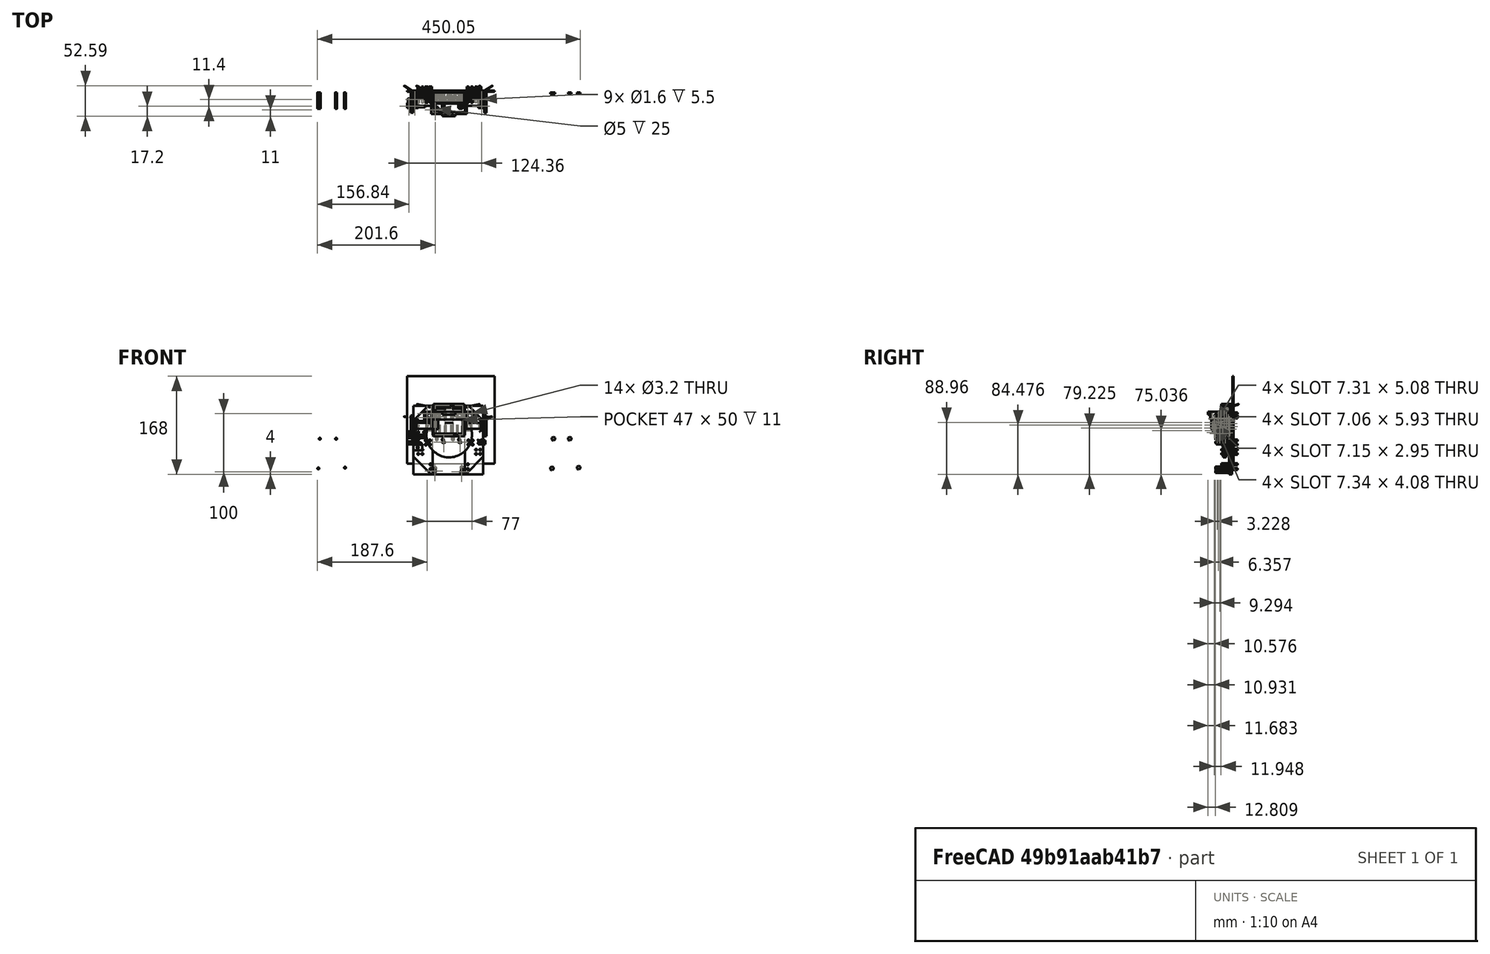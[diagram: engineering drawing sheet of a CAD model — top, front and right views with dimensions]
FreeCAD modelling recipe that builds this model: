
FCSTD DOCUMENT  (FreeCAD 0.17R13522 (Git))
Label: 5028.6 Blank Frank
License: All rights reserved
LicenseURL: http://en.wikipedia.org/wiki/All_rights_reserved
objects: Part::Cylinder×133, Part::Box×78, Part::Fuse×69, Part::Cut×66, Part::Feature×37, Part::MultiFuse×31, Part::Fillet×15, Part::Mirroring×14, Part::Chamfer×10, Part::Cone×9, Part::Compound×3, Part::Torus×2, App::DocumentObjectGroup×1
note: 467 computed .brp shape members not serialized (recipe doc carries the construction recipe); baked Part::Feature solids carry a one-line shape summary decoded from their .brp

FEATURE [Part::Cylinder] Cylinder
  Angle = 360
  AttacherType = Attacher::AttachEngine3D
  Height = 30
  Radius = 7
FEATURE [Part::Cylinder] Cylinder001
  Angle = 360
  AttacherType = Attacher::AttachEngine3D
  Height = 19
  Placement = pos=(0,0,30) rot=(0,0,1;0rad)
  Radius = 7
FEATURE [Part::Cylinder] Cylinder002
  Angle = 360
  AttacherType = Attacher::AttachEngine3D
  Height = 1.8
  Placement = pos=(0,0,49) rot=(0,0,1;0rad)
  Radius = 2.5
FEATURE [Part::Compound] Compound
  Links = -> [Cylinder,Cylinder002,Cylinder001]
FEATURE [Part::Cylinder] Cylinder003
  Angle = 360
  AttacherType = Attacher::AttachEngine3D
  Height = 30
  Radius = 7
FEATURE [Part::Cylinder] Cylinder004
  Angle = 360
  AttacherType = Attacher::AttachEngine3D
  Height = 19
  Placement = pos=(0,0,30) rot=(0,0,1;0rad)
  Radius = 7
FEATURE [Part::Cylinder] Cylinder005
  Angle = 360
  AttacherType = Attacher::AttachEngine3D
  Height = 1.8
  Placement = pos=(0,0,49) rot=(0,0,1;0rad)
  Radius = 2.5
FEATURE [Part::Compound] Compound001
  Links = -> [Cylinder003,Cylinder005,Cylinder004]
  Placement = pos=(14.5,0,50) rot=(1,0,0;3.14159rad)
FEATURE [Part::Cylinder] Cylinder006
  Angle = 360
  AttacherType = Attacher::AttachEngine3D
  Height = 30
  Radius = 7
FEATURE [Part::Cylinder] Cylinder007
  Angle = 360
  AttacherType = Attacher::AttachEngine3D
  Height = 19
  Placement = pos=(0,0,30) rot=(0,0,1;0rad)
  Radius = 7
FEATURE [Part::Cylinder] Cylinder008
  Angle = 360
  AttacherType = Attacher::AttachEngine3D
  Height = 1.8
  Placement = pos=(0,0,49) rot=(0,0,1;0rad)
  Radius = 2.5
FEATURE [Part::Compound] Compound002
  Links = -> [Cylinder006,Cylinder008,Cylinder007]
  Placement = pos=(29,0,0) rot=(0,0,1;0rad)
FEATURE [Part::Box] Box  label="Cube"
  AttacherType = Attacher::AttachEngine3D
  Height = 50
  Length = 47
  Placement = pos=(-9,-8,0) rot=(0,0,1;0rad)
  Width = 12
FEATURE [Part::Box] Box001  label="Cube001"
  AttacherType = Attacher::AttachEngine3D
  Height = 55
  Length = 53
  Placement = pos=(-12,-8,-2.5) rot=(0,0,1;0rad)
  Width = 11
FEATURE [Part::Cylinder] Cylinder009
  Angle = 360
  AttacherType = Attacher::AttachEngine3D
  Height = 50
  Radius = 7
FEATURE [Part::Cylinder] Cylinder010
  Angle = 360
  AttacherType = Attacher::AttachEngine3D
  Height = 50
  Placement = pos=(14.5,0,0) rot=(0,0,1;0rad)
  Radius = 7
FEATURE [Part::Cut] Cut
  Base = -> Box001
  Tool = -> Box
FEATURE [Part::Box] Box002  label="Cube002"
  AttacherType = Attacher::AttachEngine3D
  Height = 55
  Length = 53
  Placement = pos=(-12,3,-2.5) rot=(0,0,1;0rad)
  Width = 7
FEATURE [Part::Fuse] Fusion
  Base = -> Cut
  Tool = -> Box002
FEATURE [Part::Cut] Cut001  label="No idea why this is here...."
  Base = -> Fusion
  Tool = -> Cylinder009
FEATURE [Part::Cylinder] Cylinder011
  Angle = 360
  AttacherType = Attacher::AttachEngine3D
  Height = 50
  Placement = pos=(29,0,0) rot=(0,0,1;0rad)
  Radius = 7
FEATURE [Part::Box] Box003  label="Cube003"
  AttacherType = Attacher::AttachEngine3D
  Height = 5
  Length = 2
  Placement = pos=(28,-9,-2) rot=(0,0,1;0rad)
  Width = 12
FEATURE [Part::Box] Box004  label="Cube004"
  AttacherType = Attacher::AttachEngine3D
  Height = 5
  Length = 2
  Placement = pos=(18.5,-9,46) rot=(0,0,1;0rad)
  Width = 12
FEATURE [Part::Box] Box005  label="Cube005"
  AttacherType = Attacher::AttachEngine3D
  Height = 5
  Length = 2
  Placement = pos=(-2,-9,46) rot=(0,0,1;0rad)
  Width = 12
FEATURE [Part::Box] Box006  label="Cube006"
  AttacherType = Attacher::AttachEngine3D
  Height = 5
  Length = 3
  Placement = pos=(35,-9,-4) rot=(0,0,1;0rad)
  Width = 12
FEATURE [Part::Cut] Cut008
FEATURE [Part::Torus] Torus001
  Angle1 = -180
  Angle2 = 180
  Angle3 = 360
  AttacherType = Attacher::AttachEngine3D
  Placement = pos=(0,0,2) rot=(0,0,1;0rad)
  Radius1 = 19
  Radius2 = 1.5
FEATURE [Part::Cut] Cut009  label="wheel2"
  Base = -> Cut008
  Placement = pos=(75,-7,15) rot=(0,1,0;1.5708rad)
  Tool = -> Torus001
FEATURE [Part::Torus] Torus
  Angle1 = -180
  Angle2 = 180
  Angle3 = 360
  AttacherType = Attacher::AttachEngine3D
  Placement = pos=(0,0,2) rot=(0,0,1;0rad)
  Radius1 = 19
  Radius2 = 1.5
FEATURE [Part::Cut] Cut010
FEATURE [Part::Cut] Cut011  label="wheel1"
  Base = -> Cut010
  Placement = pos=(-51,-7,15) rot=(0,1,0;1.5708rad)
  Tool = -> Torus
FEATURE [Part::Fuse] Fusion003
FEATURE [Part::Cylinder] Cylinder012
  Angle = 360
  AttacherType = Attacher::AttachEngine3D
  Height = 10
  Placement = pos=(5,-4.5,0) rot=(0,1,0;1.5708rad)
  Radius = 0.8
FEATURE [Part::Fuse] Fusion048  label="right-motor001"
  Base = -> Cylinder012
  Placement = pos=(-51,-7,15) rot=(0,0,1;0rad)
  Tool = -> Fusion003
FEATURE [Part::Fuse] Fusion049
FEATURE [Part::Cylinder] Cylinder013
  Angle = 360
  AttacherType = Attacher::AttachEngine3D
  Height = 10
  Placement = pos=(5,-4.5,0) rot=(0,1,0;1.5708rad)
  Radius = 0.8
FEATURE [Part::Fuse] Fusion050  label="left-motor001"
  Base = -> Cylinder013
  Placement = pos=(79,-7,15) rot=(0,0,1;3.14159rad)
  Tool = -> Fusion049
FEATURE [Part::Box] Box007  label="Cube007"
  AttacherType = Attacher::AttachEngine3D
  Height = 5
  Length = 2
  Placement = pos=(37.5,-9,46) rot=(0,0,1;0rad)
  Width = 12
FEATURE [Part::Box] Box008  label="Cube008"
  AttacherType = Attacher::AttachEngine3D
  Height = 5
  Length = 2
  Placement = pos=(8,-9,-2) rot=(0,0,1;0rad)
  Width = 12
FEATURE [Part::Box] Box009  label="The Ground"
  AttacherType = Attacher::AttachEngine3D
  Height = 150
  Length = 150
  Placement = pos=(-57,11,-50) rot=(0,0,1;0rad)
  Width = 2
FEATURE [Part::Box] Box010  label="Motor Mount Left"
  AttacherType = Attacher::AttachEngine3D
  Height = 16
  Length = 4
  Placement = pos=(69,-13,7) rot=(0,0,1;0rad)
  Width = 20
FEATURE [Part::Box] Box011  label="Motor Mount Right"
  AttacherType = Attacher::AttachEngine3D
  Height = 16
  Length = 4
  Placement = pos=(-46,-13,7) rot=(0,0,1;0rad)
  Width = 20
FEATURE [Part::Box] Box012  label="Motor Support Right"
  AttacherType = Attacher::AttachEngine3D
  Height = 16
  Length = 10
  Placement = pos=(-25,-1,7) rot=(0,0,1;0rad)
  Width = 8
FEATURE [Part::Box] Box013  label="Motor Support Left"
  AttacherType = Attacher::AttachEngine3D
  Height = 16
  Length = 10
  Placement = pos=(43,-1,7) rot=(0,0,1;0rad)
  Width = 8
FEATURE [Part::Cylinder] Cylinder014
  Angle = 360
  AttacherType = Attacher::AttachEngine3D
  Height = 28
  Placement = pos=(40.7,0,-10.3) rot=(1,0,0;1.5708rad)
  Radius = 1.6
FEATURE [Part::Cylinder] Cylinder015
  Angle = 360
  AttacherType = Attacher::AttachEngine3D
  Height = 28
  Placement = pos=(-2.4,0,-59.8) rot=(1,0,0;1.5708rad)
  Radius = 1.6
FEATURE [Part::Cylinder] Cylinder016
  Angle = 360
  AttacherType = Attacher::AttachEngine3D
  Height = 28
  Placement = pos=(-5,0,-9) rot=(1,0,0;1.5708rad)
  Radius = 1.6
FEATURE [Part::Cylinder] Cylinder017
  Angle = 360
  AttacherType = Attacher::AttachEngine3D
  Height = 28
  Placement = pos=(25.5,0,-59.8) rot=(1,0,0;1.5708rad)
  Radius = 1.6
FEATURE [Part::Fuse] Fusion051
  Base = -> Cylinder015
  Tool = -> Cylinder016
FEATURE [Part::Fuse] Fusion052
  Base = -> Cylinder014
  Tool = -> Cylinder017
FEATURE [Part::Fuse] Fusion053  label="Screw holes on Arduino Duo"
  Base = -> Fusion051
  Tool = -> Fusion052
FEATURE [Part::Mirroring] Part__Mirroring  label="XXXXXScrew holes on Arduino Duo (Mirror #1)"
  Base = (0,0,0)
  Normal = (0,0,1)
  Placement = pos=(-204,10,-67) rot=(0,0,1;0rad)
  Source = -> Fusion053
FEATURE [Part::Box] Box014  label="Not used Cube"
  AttacherType = Attacher::AttachEngine3D
  Height = 10
  Length = 10
  Placement = pos=(-1,4,-5.85) rot=(0,0,1;0rad)
  Width = 10
FEATURE [Part::Box] Box015  label="Cube014 Arduino Support cube"
  AttacherType = Attacher::AttachEngine3D
  Height = 67
  Length = 55
  Placement = pos=(-13,5,-68) rot=(0,0,1;0rad)
  Width = 5
FEATURE [Part::Cylinder] Cylinder018
  Angle = 360
  AttacherType = Attacher::AttachEngine3D
  Height = 5
  Placement = pos=(15,0,0) rot=(1,0,0;1.5708rad)
  Radius = 39
FEATURE [Part::Cut] Cut014  label="M3 Nut"
  Base = -> Cut001
  Placement = pos=(-6.4,10,-7.2) rot=(1,0,0;1.5708rad)
  Tool = -> Cylinder001
FEATURE [Part::Cut] Cut015  label="M3 Nut001"
  Base = -> Cut001
  Placement = pos=(21.5,10,-7.2) rot=(1,0,0;1.5708rad)
  Tool = -> Cylinder001
FEATURE [Part::Cut] Cut016  label="M3 Nut002"
  Base = -> Cut001
  Placement = pos=(36.7,10,-56.7) rot=(1,0,0;1.5708rad)
  Tool = -> Cylinder001
FEATURE [Part::Cut] Cut017  label="M3 Nut003"
  Base = -> Cut001
  Placement = pos=(-9,10,-58) rot=(1,0,0;1.5708rad)
  Tool = -> Cylinder001
FEATURE [Part::Cut] Cut018
  Base = -> Cut
  Placement = pos=(-9,10,-58) rot=(1,0,0;1.5708rad)
  Tool = -> Box006
FEATURE [Part::Cut] Cut019
  Base = -> Cut
  Placement = pos=(36.7,10,-56.7) rot=(1,0,0;1.5708rad)
  Tool = -> Box006
FEATURE [Part::Cut] Cut020
  Base = -> Cut
  Placement = pos=(-6.4,10,-7.2) rot=(1,0,0;1.5708rad)
  Tool = -> Box006
FEATURE [Part::Cut] Cut021
  Base = -> Cut
  Placement = pos=(21.5,10,-7.2) rot=(1,0,0;1.5708rad)
  Tool = -> Box006
FEATURE [Part::MultiFuse] Fusion054  label="XXXXXHex Holes"
  Placement = pos=(200,0,0) rot=(0,0,1;0rad)
  Shapes = -> [Cut018,Cut021,Cut019,Cut020]
FEATURE [Part::Box] Box016  label="Cube015"
  AttacherType = Attacher::AttachEngine3D
  Height = 117
  Length = 33
  Placement = pos=(-46,7,-68) rot=(0,0,1;0rad)
  Width = 3
FEATURE [Part::Box] Box017  label="Cube016"
  AttacherType = Attacher::AttachEngine3D
  Height = 117
  Length = 31
  Placement = pos=(42,7,-68) rot=(0,0,1;0rad)
  Width = 3
FEATURE [Part::Cylinder] Cylinder019
  Angle = 360
  AttacherType = Attacher::AttachEngine3D
  Height = 28
  Placement = pos=(48,20,-10) rot=(1,0,0;1.5708rad)
  Radius = 1.6
FEATURE [Part::Cylinder] Cylinder020
  Angle = 360
  AttacherType = Attacher::AttachEngine3D
  Height = 28
  Placement = pos=(47,20,-51) rot=(1,0,0;1.5708rad)
  Radius = 1.6
FEATURE [Part::Cylinder] Cylinder021
  Angle = 360
  AttacherType = Attacher::AttachEngine3D
  Height = 28
  Placement = pos=(48,20,-17) rot=(1,0,0;1.5708rad)
  Radius = 1.6
FEATURE [Part::Cylinder] Cylinder022
  Angle = 360
  AttacherType = Attacher::AttachEngine3D
  Height = 28
  Placement = pos=(47,20,-59) rot=(1,0,0;1.5708rad)
  Radius = 1.6
FEATURE [Part::Cylinder] Cylinder023
  Angle = 360
  AttacherType = Attacher::AttachEngine3D
  Height = 28
  Placement = pos=(55,20,-17) rot=(1,0,0;1.5708rad)
  Radius = 1.6
FEATURE [Part::Cylinder] Cylinder024
  Angle = 360
  AttacherType = Attacher::AttachEngine3D
  Height = 28
  Placement = pos=(55,20,-10) rot=(1,0,0;1.5708rad)
  Radius = 1.6
FEATURE [Part::MultiFuse] Fusion055
  Shapes = -> [Cylinder021,Cylinder023,Cylinder024,Cylinder019]
FEATURE [Part::MultiFuse] Fusion056
  Placement = pos=(13,0,-16) rot=(0,0,1;0rad)
  Shapes = -> [Cylinder021,Cylinder023,Cylinder024,Cylinder019]
FEATURE [Part::MultiFuse] Fusion057  label="Mount holes top left"
  Placement = pos=(-1,0,46) rot=(0,0,1;0rad)
  Shapes = -> [Cylinder021,Cylinder023,Cylinder024,Cylinder019]
FEATURE [Part::MultiFuse] Fusion058  label="Mount holes top right"
  Placement = pos=(-71,0,46) rot=(0,0,1;0rad)
  Shapes = -> [Cylinder021,Cylinder023,Cylinder024,Cylinder019]
FEATURE [Part::MultiFuse] Fusion059
  Shapes = -> [Cylinder022,Cylinder020,Fusion055,Fusion056]
FEATURE [Part::Mirroring] Part__Mirroring001  label="Mount holes bottom right"
  Base = (0,0,0)
  Normal = (1,0,0)
  Placement = pos=(30,0,0) rot=(0,0,1;0rad)
  Source = -> Fusion059
FEATURE [Part::Cylinder] Cylinder025
  Angle = 360
  AttacherType = Attacher::AttachEngine3D
  Height = 28
  Placement = pos=(48,20,-10) rot=(1,0,0;1.5708rad)
  Radius = 1.6
FEATURE [Part::Cylinder] Cylinder026
  Angle = 360
  AttacherType = Attacher::AttachEngine3D
  Height = 28
  Placement = pos=(47,20,-51) rot=(1,0,0;1.5708rad)
  Radius = 1.6
FEATURE [Part::Cylinder] Cylinder027
  Angle = 360
  AttacherType = Attacher::AttachEngine3D
  Height = 28
  Placement = pos=(48,20,-17) rot=(1,0,0;1.5708rad)
  Radius = 1.6
FEATURE [Part::Cylinder] Cylinder028
  Angle = 360
  AttacherType = Attacher::AttachEngine3D
  Height = 28
  Placement = pos=(47,20,-59) rot=(1,0,0;1.5708rad)
  Radius = 1.6
FEATURE [Part::Cylinder] Cylinder029
  Angle = 360
  AttacherType = Attacher::AttachEngine3D
  Height = 28
  Placement = pos=(55,20,-17) rot=(1,0,0;1.5708rad)
  Radius = 1.6
FEATURE [Part::Cylinder] Cylinder030
  Angle = 360
  AttacherType = Attacher::AttachEngine3D
  Height = 28
  Placement = pos=(55,20,-10) rot=(1,0,0;1.5708rad)
  Radius = 1.6
FEATURE [Part::MultiFuse] Fusion060
  Shapes = -> [Cylinder027,Cylinder029,Cylinder030,Cylinder025]
FEATURE [Part::MultiFuse] Fusion061
  Placement = pos=(13,0,-16) rot=(0,0,1;0rad)
  Shapes = -> [Cylinder027,Cylinder029,Cylinder030,Cylinder025]
FEATURE [Part::MultiFuse] Fusion062  label="Mount holes bottom left"
  Shapes = -> [Cylinder028,Cylinder026,Fusion060,Fusion061]
FEATURE [Part::Cylinder] Cylinder031  label="Cylinder127"
  Angle = 360
  AttacherType = Attacher::AttachEngine3D
  Height = 10
  Placement = pos=(0,18,29) rot=(0,0,1;0rad)
  Radius = 2.25
FEATURE [Part::Cylinder] Cylinder032  label="Cylinder128"
  Angle = 360
  AttacherType = Attacher::AttachEngine3D
  Height = 10
  Placement = pos=(4.5,18,32) rot=(0,0,1;0rad)
  Radius = 1
FEATURE [Part::Cylinder] Cylinder033  label="Cylinder129"
  Angle = 360
  AttacherType = Attacher::AttachEngine3D
  Height = 10
  Placement = pos=(-4.5,18,32) rot=(0,0,1;0rad)
  Radius = 1
FEATURE [Part::Fuse] Fusion009  label="Mounting Screw Holes"
  Base = -> Cylinder032
  Tool = -> Cylinder033
FEATURE [Part::Fuse] Fusion071  label="Motor Holes Left"
  Base = -> Cylinder031
  Placement = pos=(37,-7,-3) rot=(0.57735,0.57735,0.57735;2.0944rad)
  Tool = -> Fusion009
FEATURE [Part::Cylinder] Cylinder034  label="Cylinder130"
  Angle = 360
  AttacherType = Attacher::AttachEngine3D
  Height = 10
  Placement = pos=(0,18,29) rot=(0,0,1;0rad)
  Radius = 2.25
FEATURE [Part::Cylinder] Cylinder035  label="Cylinder131"
  Angle = 360
  AttacherType = Attacher::AttachEngine3D
  Height = 10
  Placement = pos=(4.5,18,32) rot=(0,0,1;0rad)
  Radius = 1
FEATURE [Part::Cylinder] Cylinder036  label="Cylinder132"
  Angle = 360
  AttacherType = Attacher::AttachEngine3D
  Height = 10
  Placement = pos=(-4.5,18,32) rot=(0,0,1;0rad)
  Radius = 1
FEATURE [Part::Fuse] Fusion072  label="Mounting Screw Holes001"
  Base = -> Cylinder035
  Tool = -> Cylinder036
FEATURE [Part::Fuse] Fusion073  label="Motor Holes Right"
  Base = -> Cylinder034
  Placement = pos=(-79,-7,-3) rot=(0.57735,0.57735,0.57735;2.0944rad)
  Tool = -> Fusion072
FEATURE [Part::Cylinder] Cylinder037  label="Cylinder133"
  Angle = 360
  AttacherType = Attacher::AttachEngine3D
  Height = 28
  Placement = pos=(40.7,0,-10.3) rot=(1,0,0;1.5708rad)
  Radius = 1.6
FEATURE [Part::Cylinder] Cylinder038  label="Cylinder134"
  Angle = 360
  AttacherType = Attacher::AttachEngine3D
  Height = 28
  Placement = pos=(-2.4,0,-59.8) rot=(1,0,0;1.5708rad)
  Radius = 1.6
FEATURE [Part::Cylinder] Cylinder039  label="Cylinder135"
  Angle = 360
  AttacherType = Attacher::AttachEngine3D
  Height = 28
  Placement = pos=(-5,0,-9) rot=(1,0,0;1.5708rad)
  Radius = 1.6
FEATURE [Part::Cylinder] Cylinder040  label="Cylinder136"
  Angle = 360
  AttacherType = Attacher::AttachEngine3D
  Height = 28
  Placement = pos=(25.5,0,-59.8) rot=(1,0,0;1.5708rad)
  Radius = 1.6
FEATURE [Part::Fuse] Fusion074
  Base = -> Cylinder038
  Tool = -> Cylinder039
FEATURE [Part::Fuse] Fusion075
  Base = -> Cylinder037
  Tool = -> Cylinder040
FEATURE [Part::Fuse] Fusion076  label="Screw holes on Arduino Duo001"
  Base = -> Fusion074
  Tool = -> Fusion075
FEATURE [Part::Mirroring] Part__Mirroring002  label="Screw holes on Arduino Duo (Mirror #1)001"
  Base = (0,0,0)
  Normal = (0,0,1)
  Placement = pos=(-4,10,-67) rot=(0,0,1;0rad)
  Source = -> Fusion076
FEATURE [Part::Mirroring] Part__Mirroring003  label="Screw holes on Arduino Duo (Mirror #1)001 (Mirror #4)"
  Base = (0,0,0)
  Normal = (1,0,0)
  Placement = pos=(27,0,-6) rot=(0,0,1;0rad)
  Source = -> Part__Mirroring002
FEATURE [Part::Box] Box018  label="Cube017"
  AttacherType = Attacher::AttachEngine3D
  Height = 50
  Length = 47
  Placement = pos=(-9,-8,0) rot=(0,0,1;0rad)
  Width = 12
FEATURE [Part::Box] Box019  label="Cube018"
  AttacherType = Attacher::AttachEngine3D
  Height = 55
  Length = 53
  Placement = pos=(-12,-8,-2.5) rot=(0,0,1;0rad)
  Width = 11
FEATURE [Part::Cut] Cut031
  Base = -> Box019
  Tool = -> Box018
FEATURE [Part::Box] Box020  label="Cube019"
  AttacherType = Attacher::AttachEngine3D
  Height = 5
  Length = 3
  Placement = pos=(35,-9,-4) rot=(0,0,1;0rad)
  Width = 12
FEATURE [Part::Cut] Cut032
  Base = -> Cut031
  Placement = pos=(-9,10,-58) rot=(1,0,0;1.5708rad)
  Tool = -> Box020
FEATURE [Part::Cut] Cut033
  Base = -> Cut031
  Placement = pos=(36.7,10,-56.7) rot=(1,0,0;1.5708rad)
  Tool = -> Box020
FEATURE [Part::Cut] Cut034
  Base = -> Cut031
  Placement = pos=(-6.4,10,-7.2) rot=(1,0,0;1.5708rad)
  Tool = -> Box020
FEATURE [Part::Cut] Cut035
  Base = -> Cut031
  Placement = pos=(21.5,10,-7.2) rot=(1,0,0;1.5708rad)
  Tool = -> Box020
FEATURE [Part::MultiFuse] Fusion077
  Shapes = -> [Cut032,Cut035,Cut033,Cut034]
FEATURE [Part::Mirroring] Part__Mirroring004  label="Hex Holes"
  Base = (0,0,0)
  Normal = (1,0,0)
  Placement = pos=(27,0,-6) rot=(0,0,1;0rad)
  Source = -> Fusion077
FEATURE [Part::Box] Box021  label="Cube020"
  AttacherType = Attacher::AttachEngine3D
  Height = 13
  Length = 61
  Placement = pos=(-16,-27,26) rot=(0,0,1;0rad)
  Width = 34
FEATURE [Part::Box] Box022  label="Cube021"
  AttacherType = Attacher::AttachEngine3D
  Height = 13
  Length = 12
  Placement = pos=(45,4,26) rot=(0,0,1;0rad)
  Width = 3
FEATURE [Part::Box] Box023  label="Cube022"
  AttacherType = Attacher::AttachEngine3D
  Height = 13
  Length = 12
  Placement = pos=(-28,4,26) rot=(0,0,1;0rad)
  Width = 3
FEATURE [Part::Box] Box024  label="Cube023"
  AttacherType = Attacher::AttachEngine3D
  Height = 13
  Length = 55
  Placement = pos=(-13,-24,26) rot=(0,0,1;0rad)
  Width = 31
FEATURE [Part::Cylinder] Cylinder041  label="Cylinder137"
  Angle = 360
  AttacherType = Attacher::AttachEngine3D
  Height = 28
  Placement = pos=(54,20,29) rot=(1,0,0;1.5708rad)
  Radius = 1.6
FEATURE [Part::Cylinder] Cylinder042  label="Cylinder138"
  Angle = 360
  AttacherType = Attacher::AttachEngine3D
  Height = 28
  Placement = pos=(54,20,36) rot=(1,0,0;1.5708rad)
  Radius = 1.6
FEATURE [Part::Cylinder] Cylinder043  label="Cylinder139"
  Angle = 360
  AttacherType = Attacher::AttachEngine3D
  Height = 28
  Placement = pos=(-23,20,29) rot=(1,0,0;1.5708rad)
  Radius = 1.6
FEATURE [Part::Cylinder] Cylinder044  label="Cylinder140"
  Angle = 360
  AttacherType = Attacher::AttachEngine3D
  Height = 28
  Placement = pos=(-23,20,36) rot=(1,0,0;1.5708rad)
  Radius = 1.6
FEATURE [Part::Cylinder] Cylinder045  label="Cylinder141"
  Angle = 360
  AttacherType = Attacher::AttachEngine3D
  Height = 10
  Placement = pos=(36,-17.25,32.5) rot=(0,1,0;1.5708rad)
  Radius = 2.5
FEATURE [Part::Cut] Cut037
  Base = -> Box021
  Tool = -> Box024
FEATURE [Part::Cut] Cut038
  Base = -> Cut037
  Tool = -> Cylinder045
FEATURE [Part::Box] Box025  label="Cube024"
  AttacherType = Attacher::AttachEngine3D
  Height = 5
  Length = 22
  Placement = pos=(3.5,-31,34) rot=(0,0,1;0rad)
  Width = 4
FEATURE [Part::Cylinder] Cylinder046  label="Cylinder142"
  Angle = 360
  AttacherType = Attacher::AttachEngine3D
  Height = 10
  Placement = pos=(20.75,-29,30) rot=(0,0,1;0rad)
  Radius = 0.85
FEATURE [Part::Cylinder] Cylinder047  label="Cylinder143"
  Angle = 360
  AttacherType = Attacher::AttachEngine3D
  Height = 10
  Placement = pos=(8.25,-29,40) rot=(1,0,0;3.14159rad)
  Radius = 0.85
FEATURE [Part::Fuse] Fusion078
  Base = -> Cylinder046
  Tool = -> Cylinder047
FEATURE [Part::Cut] Cut039
  Base = -> Box025
  Tool = -> Fusion078
FEATURE [Part::Fuse] Fusion079
  Base = -> Cut038
  Tool = -> Cut039
FEATURE [Part::Fuse] Fusion080
  Base = -> Cylinder043
  Tool = -> Cylinder044
FEATURE [Part::Fuse] Fusion081
  Base = -> Cylinder041
  Tool = -> Cylinder042
FEATURE [Part::Fuse] Fusion082
  Base = -> Box023
  Tool = -> Fusion079
FEATURE [Part::Fuse] Fusion083
  Base = -> Box022
  Tool = -> Fusion082
FEATURE [Part::Cut] Cut040
  Base = -> Fusion083
  Tool = -> Fusion081
FEATURE [Part::Cut] Cut041  label="Switch Bracket"
  Base = -> Cut040
  Tool = -> Fusion080
FEATURE [Part::Cylinder] Cylinder048  label="Cylinder144"
  Angle = 360
  AttacherType = Attacher::AttachEngine3D
  Height = 28
  Placement = pos=(-23,20,29) rot=(1,0,0;1.5708rad)
  Radius = 1.6
FEATURE [Part::Cylinder] Cylinder049  label="Cylinder145"
  Angle = 360
  AttacherType = Attacher::AttachEngine3D
  Height = 28
  Placement = pos=(-23,20,36) rot=(1,0,0;1.5708rad)
  Radius = 1.6
FEATURE [Part::Fuse] Fusion084
  Base = -> Cylinder048
  Placement = pos=(1,0,0) rot=(0,0,1;0rad)
  Tool = -> Cylinder049
FEATURE [Part::Cylinder] Cylinder050  label="Cylinder146"
  Angle = 360
  AttacherType = Attacher::AttachEngine3D
  Height = 28
  Placement = pos=(-23,20,29) rot=(1,0,0;1.5708rad)
  Radius = 1.6
FEATURE [Part::Cylinder] Cylinder051  label="Cylinder147"
  Angle = 360
  AttacherType = Attacher::AttachEngine3D
  Height = 28
  Placement = pos=(-23,20,36) rot=(1,0,0;1.5708rad)
  Radius = 1.6
FEATURE [Part::Fuse] Fusion085
  Base = -> Cylinder050
  Placement = pos=(-1,0,0) rot=(0,0,1;0rad)
  Tool = -> Cylinder051
FEATURE [Part::Cut] Cut042
  Base = -> Cut041
  Tool = -> Fusion084
FEATURE [Part::Cut] Cut043  label="Switch Bracket001"
  Base = -> Cut042
  Tool = -> Fusion085
FEATURE [Part::Cylinder] Cylinder052  label="Cylinder148"
  Angle = 360
  AttacherType = Attacher::AttachEngine3D
  Height = 42
  Radius = 4.8
FEATURE [Part::Cylinder] Cylinder053  label="Cylinder149"
  Angle = 360
  AttacherType = Attacher::AttachEngine3D
  Height = 1.6
  Placement = pos=(0,0,42) rot=(0,0,1;0rad)
  Radius = 1.65
FEATURE [Part::Fuse] Fusion086
  Base = -> Cylinder052
  Placement = pos=(2,0,0) rot=(0,0,1;0rad)
  Tool = -> Cylinder053
FEATURE [Part::Cylinder] Cylinder054  label="Cylinder150"
  Angle = 360
  AttacherType = Attacher::AttachEngine3D
  Height = 42
  Radius = 4.8
FEATURE [Part::Cylinder] Cylinder055  label="Cylinder151"
  Angle = 360
  AttacherType = Attacher::AttachEngine3D
  Height = 1.6
  Placement = pos=(0,0,42) rot=(0,0,1;0rad)
  Radius = 1.65
FEATURE [Part::Fuse] Fusion087
  Base = -> Cylinder054
  Placement = pos=(12,0,0) rot=(0,0,1;0rad)
  Tool = -> Cylinder055
FEATURE [Part::Cylinder] Cylinder056  label="Cylinder152"
  Angle = 360
  AttacherType = Attacher::AttachEngine3D
  Height = 42
  Radius = 4.8
FEATURE [Part::Cylinder] Cylinder057  label="Cylinder153"
  Angle = 360
  AttacherType = Attacher::AttachEngine3D
  Height = 1.6
  Placement = pos=(0,0,42) rot=(0,0,1;0rad)
  Radius = 1.65
FEATURE [Part::Fuse] Fusion088
  Base = -> Cylinder056
  Placement = pos=(22,0,0) rot=(0,0,1;0rad)
  Tool = -> Cylinder057
FEATURE [Part::Cylinder] Cylinder058  label="Cylinder154"
  Angle = 360
  AttacherType = Attacher::AttachEngine3D
  Height = 42
  Radius = 4.8
FEATURE [Part::Cylinder] Cylinder059  label="Cylinder155"
  Angle = 360
  AttacherType = Attacher::AttachEngine3D
  Height = 1.6
  Placement = pos=(0,0,42) rot=(0,0,1;0rad)
  Radius = 1.65
FEATURE [Part::Fuse] Fusion089
  Base = -> Cylinder058
  Placement = pos=(32,0,0) rot=(0,0,1;0rad)
  Tool = -> Cylinder059
FEATURE [Part::Cylinder] Cylinder060  label="Cylinder156"
  Angle = 360
  AttacherType = Attacher::AttachEngine3D
  Height = 42
  Radius = 4.8
FEATURE [Part::Cylinder] Cylinder061  label="Cylinder157"
  Angle = 360
  AttacherType = Attacher::AttachEngine3D
  Height = 1.6
  Placement = pos=(0,0,42) rot=(0,0,1;0rad)
  Radius = 1.65
FEATURE [Part::Fuse] Fusion093
  Base = -> Cylinder060
  Placement = pos=(-8,0,0) rot=(0,0,1;0rad)
  Tool = -> Cylinder061
FEATURE [Part::MultiFuse] Fusion094  label="AAA Batts"
  Placement = pos=(2.5,0,2) rot=(0,0,1;0rad)
  Shapes = -> [Fusion093,Fusion086,Fusion087,Fusion088,Fusion089]
FEATURE [Part::Cylinder] Cylinder062  label="Cylinder158"
  Angle = 360
  AttacherType = Attacher::AttachEngine3D
  Height = 10
  Radius = 17
FEATURE [Part::Cylinder] Cylinder063  label="Cylinder159"
  Angle = 360
  AttacherType = Attacher::AttachEngine3D
  Height = 16
  Placement = pos=(0,0,-4) rot=(0,0,1;0rad)
  Radius = 10
FEATURE [Part::Cut] Cut044
  Base = -> Cylinder062
  Tool = -> Cylinder063
FEATURE [Part::Box] Box026  label="Cube025"
  AttacherType = Attacher::AttachEngine3D
  Height = 20
  Length = 18
  Placement = pos=(0,0,-5) rot=(0,0,1;0rad)
  Width = 20
FEATURE [Part::Box] Box027  label="Cube026"
  AttacherType = Attacher::AttachEngine3D
  Height = 20
  Length = 10
  Placement = pos=(0,0,-5) rot=(0,0,1;0.174533rad)
  Width = 20
FEATURE [Part::Cut] Cut045
  Base = -> Box027
  Tool = -> Box026
FEATURE [Part::Feature] Cut045001
  Placement = pos=(0,0,0) rot=(0,0,1;0.349066rad)
  shape: bbox 10 x 22.32 x 20 mm, 7 faces (baked)
FEATURE [Part::Feature] Cut045002
  Placement = pos=(0,0,0) rot=(0,0,1;0.698132rad)
  shape: bbox 15.32 x 20.52 x 20 mm, 7 faces (baked)
FEATURE [Part::Feature] Cut045003
  Placement = pos=(0,0,0) rot=(0,0,1;1.0472rad)
  shape: bbox 18.79 x 16.24 x 20 mm, 7 faces (baked)
FEATURE [Part::Feature] Cut045004
  Placement = pos=(0,0,0) rot=(0,0,1;1.39626rad)
  shape: bbox 20 x 10 x 20 mm, 7 faces (baked)
FEATURE [Part::Feature] Cut045005
  Placement = pos=(0,0,0) rot=(0,0,1;1.74533rad)
  shape: bbox 22.21 x 9.894 x 20 mm, 7 faces (baked)
FEATURE [Part::Feature] Cut045006
  Placement = pos=(0,0,0) rot=(0,0,1;2.0944rad)
  shape: bbox 21.75 x 12.86 x 20 mm, 7 faces (baked)
FEATURE [Part::Feature] Cut045007
  Placement = pos=(0,0,0) rot=(0,0,1;2.44346rad)
  shape: bbox 18.66 x 17.32 x 20 mm, 7 faces (baked)
FEATURE [Part::Feature] Cut045008
  Placement = pos=(0,0,0) rot=(0,0,1;2.79253rad)
  shape: bbox 13.32 x 19.7 x 20 mm, 7 faces (baked)
FEATURE [Part::Feature] Cut045009
  Placement = pos=(0,0,0) rot=(0,0,1;3.14159rad)
  shape: bbox 10.1 x 21.43 x 20 mm, 7 faces (baked)
FEATURE [Part::Feature] Cut045010
  Placement = pos=(0,0,0) rot=(0,0,1;3.49066rad)
  shape: bbox 10 x 22.32 x 20 mm, 7 faces (baked)
FEATURE [Part::Feature] Cut045011
  Placement = pos=(0,0,0) rot=(0,0,1;3.83972rad)
  shape: bbox 15.32 x 20.52 x 20 mm, 7 faces (baked)
FEATURE [Part::Feature] Cut045012
  Placement = pos=(0,0,0) rot=(0,0,1;4.18879rad)
  shape: bbox 18.79 x 16.24 x 20 mm, 7 faces (baked)
FEATURE [Part::Feature] Cut045013
  Placement = pos=(0,0,0) rot=(0,0,-1;1.74533rad)
  shape: bbox 20 x 10 x 20 mm, 7 faces (baked)
FEATURE [Part::Feature] Cut045014
  Placement = pos=(0,0,0) rot=(0,0,-1;1.39626rad)
  shape: bbox 22.21 x 9.894 x 20 mm, 7 faces (baked)
FEATURE [Part::Feature] Cut045015
  Placement = pos=(0,0,0) rot=(0,0,-1;1.0472rad)
  shape: bbox 21.75 x 12.86 x 20 mm, 7 faces (baked)
FEATURE [Part::Feature] Cut045016
  Placement = pos=(0,0,0) rot=(0,0,-1;0.698132rad)
  shape: bbox 18.66 x 17.32 x 20 mm, 7 faces (baked)
FEATURE [Part::Feature] Cut045017
  Placement = pos=(0,0,0) rot=(0,0,-1;0.349066rad)
  shape: bbox 13.32 x 19.7 x 20 mm, 7 faces (baked)
FEATURE [Part::MultiFuse] Fusion095
  Shapes = -> [Cut045001,Cut045008,Cut045010,Cut045009,Cut045005,Cut045003,Cut045006,Cut045002,Cut045004,Cut045007,Cut045016,Cut045017,Cut045011,Cut045012,Cut045013,Cut045014,Cut045015,Cut045]
FEATURE [Part::Cut] Cut045018
  Base = -> Cut044
  Placement = pos=(72,-7,15) rot=(0,1,0;1.5708rad)
  Tool = -> Fusion095
FEATURE [Part::Cut] Cut045019  label="Wheel with Spokes AB"
  Base = -> Cut009
  Tool = -> Cut045018
FEATURE [Part::Box] Box028  label="Cube027"
  AttacherType = Attacher::AttachEngine3D
  Height = 5
  Length = 2
  Placement = pos=(37.5,-9,-2) rot=(0,0,1;0rad)
  Width = 12
FEATURE [Part::Box] Box029  label="Cube028"
  AttacherType = Attacher::AttachEngine3D
  Height = 50
  Length = 47
  Placement = pos=(-9,-8,0) rot=(0,0,1;0rad)
  Width = 12
FEATURE [Part::Box] Box030  label="Cube029"
  AttacherType = Attacher::AttachEngine3D
  Height = 55
  Length = 53
  Placement = pos=(-12,-8,-2.5) rot=(0,0,1;0rad)
  Width = 11
FEATURE [Part::Cylinder] Cylinder064  label="Cylinder160"
  Angle = 360
  AttacherType = Attacher::AttachEngine3D
  Height = 50
  Radius = 7
FEATURE [Part::Cut] Cut045020
  Base = -> Box030
  Tool = -> Box029
FEATURE [Part::Box] Box031  label="Cube030"
  AttacherType = Attacher::AttachEngine3D
  Height = 55
  Length = 53
  Placement = pos=(-12,3,-2.5) rot=(0,0,1;0rad)
  Width = 7
FEATURE [Part::Fuse] Fusion096
  Base = -> Cut045020
  Tool = -> Box031
FEATURE [Part::Box] Box032  label="Battery Base"
  AttacherType = Attacher::AttachEngine3D
  Height = 50
  Length = 55
  Placement = pos=(-13,3,-1) rot=(0,0,1;0rad)
  Width = 7
FEATURE [Part::Box] Box033  label="Cube031"
  AttacherType = Attacher::AttachEngine3D
  Height = 30
  Length = 10
  Placement = pos=(-14,-25,9) rot=(0,0,1;0rad)
  Width = 10
FEATURE [Part::Cylinder] Cylinder065  label="Cylinder161"
  Angle = 360
  AttacherType = Attacher::AttachEngine3D
  Height = 43.5
  Placement = pos=(4,0,2) rot=(0,0,1;0rad)
  Radius = 4.8
FEATURE [Part::Cylinder] Cylinder066  label="Cylinder162"
  Angle = 360
  AttacherType = Attacher::AttachEngine3D
  Height = 1.6
  Placement = pos=(4,0,44) rot=(0,0,1;0rad)
  Radius = 1.65
FEATURE [Part::Fuse] Fusion097
  Base = -> Cylinder065
  Tool = -> Cylinder066
FEATURE [Part::Cylinder] Cylinder067  label="Cylinder163"
  Angle = 360
  AttacherType = Attacher::AttachEngine3D
  Height = 43.5
  Placement = pos=(14,0,2) rot=(0,0,1;0rad)
  Radius = 4.8
FEATURE [Part::Cylinder] Cylinder068  label="Cylinder164"
  Angle = 360
  AttacherType = Attacher::AttachEngine3D
  Height = 1.6
  Placement = pos=(14,0,44) rot=(0,0,1;0rad)
  Radius = 1.65
FEATURE [Part::Fuse] Fusion098
  Base = -> Cylinder067
  Tool = -> Cylinder068
FEATURE [Part::Cylinder] Cylinder069  label="Cylinder165"
  Angle = 360
  AttacherType = Attacher::AttachEngine3D
  Height = 43.5
  Placement = pos=(24,0,2) rot=(0,0,1;0rad)
  Radius = 4.8
FEATURE [Part::Cylinder] Cylinder070  label="Cylinder166"
  Angle = 360
  AttacherType = Attacher::AttachEngine3D
  Height = 1.6
  Placement = pos=(24,0,44) rot=(0,0,1;0rad)
  Radius = 1.65
FEATURE [Part::Fuse] Fusion099
  Base = -> Cylinder069
  Tool = -> Cylinder070
FEATURE [Part::Cylinder] Cylinder071  label="Cylinder167"
  Angle = 360
  AttacherType = Attacher::AttachEngine3D
  Height = 43.5
  Placement = pos=(34,0,2) rot=(0,0,1;0rad)
  Radius = 4.8
FEATURE [Part::Cylinder] Cylinder072  label="Cylinder168"
  Angle = 360
  AttacherType = Attacher::AttachEngine3D
  Height = 1.6
  Placement = pos=(34,0,44) rot=(0,0,1;0rad)
  Radius = 1.65
FEATURE [Part::Fuse] Fusion100
  Base = -> Cylinder071
  Tool = -> Cylinder072
FEATURE [Part::Cylinder] Cylinder073  label="Cylinder169"
  Angle = 360
  AttacherType = Attacher::AttachEngine3D
  Height = 43.5
  Placement = pos=(-6,0,2) rot=(0,0,1;0rad)
  Radius = 4.8
FEATURE [Part::Cylinder] Cylinder074  label="Cylinder170"
  Angle = 360
  AttacherType = Attacher::AttachEngine3D
  Height = 1.6
  Placement = pos=(-6,0,44) rot=(0,0,1;0rad)
  Radius = 1.65
FEATURE [Part::Fuse] Fusion101
  Base = -> Cylinder073
  Tool = -> Cylinder074
FEATURE [Part::MultiFuse] Fusion102  label="AAA Batts001"
  Shapes = -> [Fusion101,Fusion097,Fusion098,Fusion099,Fusion100]
FEATURE [Part::Cylinder] Cylinder075  label="Cylinder171"
  Angle = 360
  AttacherType = Attacher::AttachEngine3D
  Height = 10
  Placement = pos=(-9,-20,4) rot=(0,0,1;0rad)
  Radius = 2.75
FEATURE [Part::Cylinder] Cylinder076  label="Cylinder172"
  Angle = 360
  AttacherType = Attacher::AttachEngine3D
  Height = 27
  Placement = pos=(-9,-20,14) rot=(0,0,1;0rad)
  Radius = 2.5
FEATURE [Part::Fuse] Fusion103  label="phototransistor hole"
  Base = -> Cylinder075
  Tool = -> Cylinder076
FEATURE [Part::Cut] Cut045021  label="Phototransistor holder"
  Base = -> Box033
  Tool = -> Fusion103
FEATURE [Part::Fuse] Fusion104  label="Switch Mount with phototransistor hole"
  Base = -> Cut043
  Tool = -> Cut045021
FEATURE [Part::Cut] Cut045022
  Base = -> Box032
  Tool = -> Fusion102
FEATURE [Part::Box] Box034  label="Cube032"
  AttacherType = Attacher::AttachEngine3D
  Height = 2.5
  Length = 55
  Placement = pos=(-13,-9,-1) rot=(0,0,1;0rad)
  Width = 12
FEATURE [Part::Box] Box035  label="Cube033"
  AttacherType = Attacher::AttachEngine3D
  Height = 2.5
  Length = 55
  Placement = pos=(-13,-9,46.5) rot=(0,0,1;0rad)
  Width = 12
FEATURE [Part::Box] Box036  label="Cube034"
  AttacherType = Attacher::AttachEngine3D
  Height = 50
  Length = 2.5
  Placement = pos=(-13,-9,-1) rot=(0,0,1;0rad)
  Width = 12
FEATURE [Part::Box] Box037  label="Cube035"
  AttacherType = Attacher::AttachEngine3D
  Height = 50
  Length = 2.5
  Placement = pos=(39.5,-9,-1) rot=(0,0,1;0rad)
  Width = 12
FEATURE [Part::MultiFuse] Fusion105
  Shapes = -> [Box034,Box036,Box037,Box035]
FEATURE [Part::Box] Box038  label="Cube036"
  AttacherType = Attacher::AttachEngine3D
  Height = 5
  Length = 2
  Placement = pos=(-10.5,-9,46) rot=(0,0,1;0rad)
  Width = 12
FEATURE [Part::Box] Box039  label="Cube037"
  AttacherType = Attacher::AttachEngine3D
  Height = 5
  Length = 2
  Placement = pos=(-10.5,-9,-2) rot=(0,0,1;0rad)
  Width = 12
FEATURE [Part::MultiFuse] Fusion106
  Shapes = -> [Box039,Box038,Box028,Box007]
FEATURE [Part::MultiFuse] Fusion107
  Shapes = -> [Box003,Box004,Box005,Box008]
FEATURE [Part::Cut] Cut045023
  Base = -> Fusion105
  Tool = -> Fusion106
FEATURE [Part::Cut] Cut045024
  Base = -> Cut045023
  Tool = -> Fusion107
FEATURE [Part::Box] Box040  label="Cube038"
  AttacherType = Attacher::AttachEngine3D
  Height = 1.6
  Length = 30
  Placement = pos=(-56,-15.5,-6) rot=(0,0,1;0rad)
  Width = 15
FEATURE [Part::Box] Box041  label="Cube039"
  AttacherType = Attacher::AttachEngine3D
  Height = 10
  Length = 14
  Placement = pos=(-56,-10.5,-4.5) rot=(0,0,1;0rad)
  Width = 6
FEATURE [Part::Box] Box042  label="Cube040"
  AttacherType = Attacher::AttachEngine3D
  Height = 10
  Length = 5.3
  Placement = pos=(-51.7,-11.5,-4.5) rot=(0,0,1;0rad)
  Width = 8
FEATURE [Part::Cut] Cut045025
  Base = -> Box041
  Tool = -> Box042
FEATURE [Part::Fuse] Fusion108  label="Spoke Sensor PCB"
  Base = -> Box040
  Tool = -> Cut045025
FEATURE [Part::Cylinder] Cylinder077  label="Cylinder173"
  Angle = 360
  AttacherType = Attacher::AttachEngine3D
  Height = 14.5
  Placement = pos=(-43.6,-2.4,-9) rot=(0,0,1;0rad)
  Radius = 0.8
FEATURE [Part::Cylinder] Cylinder078  label="Cylinder174"
  Angle = 360
  AttacherType = Attacher::AttachEngine3D
  Height = 14.5
  Placement = pos=(-43.6,-13.8,-9) rot=(0,0,1;0rad)
  Radius = 0.8
FEATURE [Part::Fuse] Fusion109
  Base = -> Cylinder077
  Tool = -> Cylinder078
FEATURE [Part::Cut] Cut045026  label="Spoke Sensor PCB001"
  Base = -> Fusion108
  Tool = -> Fusion109
FEATURE [Part::Cylinder] Cylinder079  label="Cylinder175"
  Angle = 360
  AttacherType = Attacher::AttachEngine3D
  Height = 14.5
  Placement = pos=(-43.6,-2.4,-18) rot=(0,0,1;0rad)
  Radius = 0.8
FEATURE [Part::Cylinder] Cylinder080  label="Cylinder176"
  Angle = 360
  AttacherType = Attacher::AttachEngine3D
  Height = 14.5
  Placement = pos=(-43.6,-13.8,-18) rot=(0,0,1;0rad)
  Radius = 0.8
FEATURE [Part::Fuse] Fusion110  label="Batt Holder"
  Base = -> Cut045022
  Tool = -> Cut045024
FEATURE [Part::Box] Box043  label="Cube041"
  AttacherType = Attacher::AttachEngine3D
  Height = 4
  Length = 12
  Placement = pos=(-50,-16.75,-17) rot=(0,0,1;0rad)
  Width = 23.75
FEATURE [Part::Cone] Cone
  Angle = 360
  AttacherType = Attacher::AttachEngine3D
  Height = 1.5
  Placement = pos=(-43.6,-2.4,-13) rot=(0,0,1;0rad)
  Radius1 = 2.75
  Radius2 = 1.25
FEATURE [Part::Cone] Cone001
  Angle = 360
  AttacherType = Attacher::AttachEngine3D
  Height = 1.5
  Placement = pos=(-43.6,-13.8,-13) rot=(0,0,1;0rad)
  Radius1 = 2.75
  Radius2 = 1.25
FEATURE [Part::Fuse] Fusion111
  Base = -> Cone
  Tool = -> Cone001
FEATURE [Part::Fuse] Fusion113
  Base = -> Cylinder079
  Tool = -> Cylinder080
FEATURE [Part::Cylinder] Cylinder081  label="Cylinder177"
  Angle = 360
  AttacherType = Attacher::AttachEngine3D
  Height = 14.5
  Placement = pos=(-43.6,-2.4,-18) rot=(0,0,1;0rad)
  Radius = 0.8
FEATURE [Part::Cylinder] Cylinder082  label="Cylinder178"
  Angle = 360
  AttacherType = Attacher::AttachEngine3D
  Height = 14.5
  Placement = pos=(-43.6,-13.8,-18) rot=(0,0,1;0rad)
  Radius = 0.8
FEATURE [Part::Box] Box044  label="Cube042"
  AttacherType = Attacher::AttachEngine3D
  Height = 4
  Length = 12
  Placement = pos=(-50,-16.75,-17) rot=(0,0,1;0rad)
  Width = 26.75
FEATURE [Part::Chamfer] Chamfer001
  Base = -> Box044
  Edges = 1 edges r=7: [Edge3]
FEATURE [Part::Cone] Cone002
  Angle = 360
  AttacherType = Attacher::AttachEngine3D
  Height = 1.5
  Placement = pos=(-43.6,-2.4,-13) rot=(0,0,1;0rad)
  Radius1 = 2.75
  Radius2 = 1.25
FEATURE [Part::Cone] Cone003
  Angle = 360
  AttacherType = Attacher::AttachEngine3D
  Height = 1.5
  Placement = pos=(-43.6,-13.8,-13) rot=(0,0,1;0rad)
  Radius1 = 2.75
  Radius2 = 1.25
FEATURE [Part::Fuse] Fusion114
  Base = -> Cone002
  Tool = -> Cone003
FEATURE [Part::Fuse] Fusion115
  Base = -> Chamfer001
  Tool = -> Fusion114
FEATURE [Part::Fuse] Fusion116
  Base = -> Cylinder081
  Tool = -> Cylinder082
FEATURE [Part::Cut] Cut045028
  Base = -> Fusion115
  Tool = -> Fusion116
FEATURE [Part::Mirroring] Part__Mirroring005  label="Cut045028 (Mirror #6)"
  Base = (0,0,0)
  Normal = (1,0,0)
  Placement = pos=(27,0,0) rot=(0,0,1;0rad)
  Source = -> Cut045028
FEATURE [App::DocumentObjectGroup] Group  label="Older version parts"
  Group = -> [Compound,Compound001,Compound002,Cylinder064,Cylinder010,Cylinder011,Fusion096,Part__Mirroring,Fusion054,Part__Mirroring004,Cut014,Cut015,Cut016,Cut017,Box012,Box013,Box010,Part__Mirroring005]
FEATURE [Part::Box] Box045  label="Cube043"
  AttacherType = Attacher::AttachEngine3D
  Height = 5
  Length = 2
  Placement = pos=(28,-9,-2) rot=(0,0,1;0rad)
  Width = 12
FEATURE [Part::Box] Box046  label="Cube044"
  AttacherType = Attacher::AttachEngine3D
  Height = 5
  Length = 2
  Placement = pos=(18.5,-9,46) rot=(0,0,1;0rad)
  Width = 12
FEATURE [Part::Box] Box047  label="Cube045"
  AttacherType = Attacher::AttachEngine3D
  Height = 5
  Length = 2
  Placement = pos=(-2,-9,46) rot=(0,0,1;0rad)
  Width = 12
FEATURE [Part::Box] Box048  label="Cube046"
  AttacherType = Attacher::AttachEngine3D
  Height = 5
  Length = 2
  Placement = pos=(37.5,-9,46) rot=(0,0,1;0rad)
  Width = 12
FEATURE [Part::Box] Box049  label="Cube047"
  AttacherType = Attacher::AttachEngine3D
  Height = 5
  Length = 2
  Placement = pos=(8,-9,-2) rot=(0,0,1;0rad)
  Width = 12
FEATURE [Part::Box] Box050  label="Motor Mount Left001"
  AttacherType = Attacher::AttachEngine3D
  Height = 16
  Length = 4
  Placement = pos=(69,-13,7) rot=(0,0,1;0rad)
  Width = 20
FEATURE [Part::Box] Box051  label="Motor Mount Right001"
  AttacherType = Attacher::AttachEngine3D
  Height = 16
  Length = 4
  Placement = pos=(-46,-13,7) rot=(0,0,1;0rad)
  Width = 20
FEATURE [Part::Box] Box052  label="Motor Support Right001"
  AttacherType = Attacher::AttachEngine3D
  Height = 16
  Length = 10
  Placement = pos=(-25,-1,7) rot=(0,0,1;0rad)
  Width = 8
FEATURE [Part::Box] Box053  label="Motor Support Left001"
  AttacherType = Attacher::AttachEngine3D
  Height = 16
  Length = 10
  Placement = pos=(43,-1,7) rot=(0,0,1;0rad)
  Width = 8
FEATURE [Part::Box] Box054  label="Cube014 Arduino Support cube001"
  AttacherType = Attacher::AttachEngine3D
  Height = 67
  Length = 55
  Placement = pos=(-13,5,-68) rot=(0,0,1;0rad)
  Width = 5
FEATURE [Part::Box] Box055  label="Cube048"
  AttacherType = Attacher::AttachEngine3D
  Height = 117
  Length = 33
  Placement = pos=(-46,7,-68) rot=(0,0,1;0rad)
  Width = 3
FEATURE [Part::Box] Box056  label="Cube049"
  AttacherType = Attacher::AttachEngine3D
  Height = 117
  Length = 31
  Placement = pos=(42,7,-68) rot=(0,0,1;0rad)
  Width = 3
FEATURE [Part::Cylinder] Cylinder083  label="Cylinder179"
  Angle = 360
  AttacherType = Attacher::AttachEngine3D
  Height = 28
  Placement = pos=(48,20,-10) rot=(1,0,0;1.5708rad)
  Radius = 1.6
FEATURE [Part::Cylinder] Cylinder084  label="Cylinder180"
  Angle = 360
  AttacherType = Attacher::AttachEngine3D
  Height = 28
  Placement = pos=(48,20,-17) rot=(1,0,0;1.5708rad)
  Radius = 1.6
FEATURE [Part::Cylinder] Cylinder085  label="Cylinder181"
  Angle = 360
  AttacherType = Attacher::AttachEngine3D
  Height = 28
  Placement = pos=(55,20,-17) rot=(1,0,0;1.5708rad)
  Radius = 1.6
FEATURE [Part::Cylinder] Cylinder086  label="Cylinder182"
  Angle = 360
  AttacherType = Attacher::AttachEngine3D
  Height = 28
  Placement = pos=(55,20,-10) rot=(1,0,0;1.5708rad)
  Radius = 1.6
FEATURE [Part::MultiFuse] Fusion117  label="Mount holes top left001"
  Placement = pos=(-1,0,46) rot=(0,0,1;0rad)
  Shapes = -> [Cylinder084,Cylinder085,Cylinder086,Cylinder083]
FEATURE [Part::MultiFuse] Fusion118  label="Mount holes top right001"
  Placement = pos=(-71,0,46) rot=(0,0,1;0rad)
  Shapes = -> [Cylinder084,Cylinder085,Cylinder086,Cylinder083]
FEATURE [Part::Cylinder] Cylinder087  label="Cylinder183"
  Angle = 360
  AttacherType = Attacher::AttachEngine3D
  Height = 10
  Placement = pos=(0,18,29) rot=(0,0,1;0rad)
  Radius = 2.25
FEATURE [Part::Cylinder] Cylinder088  label="Cylinder184"
  Angle = 360
  AttacherType = Attacher::AttachEngine3D
  Height = 10
  Placement = pos=(4.5,18,32) rot=(0,0,1;0rad)
  Radius = 1
FEATURE [Part::Cylinder] Cylinder089  label="Cylinder185"
  Angle = 360
  AttacherType = Attacher::AttachEngine3D
  Height = 10
  Placement = pos=(-4.5,18,32) rot=(0,0,1;0rad)
  Radius = 1
FEATURE [Part::Fuse] Fusion119  label="Mounting Screw Holes002"
  Base = -> Cylinder088
  Tool = -> Cylinder089
FEATURE [Part::Fuse] Fusion120  label="Motor Holes Left001"
  Base = -> Cylinder087
  Placement = pos=(37,-7,-3) rot=(0.57735,0.57735,0.57735;2.0944rad)
  Tool = -> Fusion119
FEATURE [Part::Cylinder] Cylinder090  label="Cylinder186"
  Angle = 360
  AttacherType = Attacher::AttachEngine3D
  Height = 10
  Placement = pos=(0,18,29) rot=(0,0,1;0rad)
  Radius = 2.25
FEATURE [Part::Cylinder] Cylinder091  label="Cylinder187"
  Angle = 360
  AttacherType = Attacher::AttachEngine3D
  Height = 10
  Placement = pos=(4.5,18,32) rot=(0,0,1;0rad)
  Radius = 1
FEATURE [Part::Cylinder] Cylinder092  label="Cylinder188"
  Angle = 360
  AttacherType = Attacher::AttachEngine3D
  Height = 10
  Placement = pos=(-4.5,18,32) rot=(0,0,1;0rad)
  Radius = 1
FEATURE [Part::Fuse] Fusion121  label="Mounting Screw Holes003"
  Base = -> Cylinder091
  Tool = -> Cylinder092
FEATURE [Part::Fuse] Fusion122  label="Motor Holes Right001"
  Base = -> Cylinder090
  Placement = pos=(-79,-7,-3) rot=(0.57735,0.57735,0.57735;2.0944rad)
  Tool = -> Fusion121
FEATURE [Part::Cylinder] Cylinder093  label="Cylinder189"
  Angle = 360
  AttacherType = Attacher::AttachEngine3D
  Height = 28
  Placement = pos=(40.7,0,-10.3) rot=(1,0,0;1.5708rad)
  Radius = 1.6
FEATURE [Part::Cylinder] Cylinder094  label="Cylinder190"
  Angle = 360
  AttacherType = Attacher::AttachEngine3D
  Height = 28
  Placement = pos=(-2.4,0,-59.8) rot=(1,0,0;1.5708rad)
  Radius = 1.6
FEATURE [Part::Cylinder] Cylinder095  label="Cylinder191"
  Angle = 360
  AttacherType = Attacher::AttachEngine3D
  Height = 28
  Placement = pos=(-5,0,-9) rot=(1,0,0;1.5708rad)
  Radius = 1.6
FEATURE [Part::Cylinder] Cylinder096  label="Cylinder192"
  Angle = 360
  AttacherType = Attacher::AttachEngine3D
  Height = 28
  Placement = pos=(25.5,0,-59.8) rot=(1,0,0;1.5708rad)
  Radius = 1.6
FEATURE [Part::Fuse] Fusion123
  Base = -> Cylinder094
  Tool = -> Cylinder095
FEATURE [Part::Fuse] Fusion124
  Base = -> Cylinder093
  Tool = -> Cylinder096
FEATURE [Part::Fuse] Fusion125  label="Screw holes on Arduino Duo002"
  Base = -> Fusion123
  Tool = -> Fusion124
FEATURE [Part::Mirroring] Part__Mirroring006  label="Screw holes on Arduino Duo (Mirror #1)002"
  Base = (0,0,0)
  Normal = (0,0,1)
  Placement = pos=(-4,10,-67) rot=(0,0,1;0rad)
  Source = -> Fusion125
FEATURE [Part::Mirroring] Part__Mirroring007  label="Screw holes on Arduino Duo (Mirror #1)001 (Mirror #4)001"
  Base = (0,0,0)
  Normal = (1,0,0)
  Placement = pos=(27,0,-6) rot=(0,0,1;0rad)
  Source = -> Part__Mirroring006
FEATURE [Part::Box] Box057  label="Cube050"
  AttacherType = Attacher::AttachEngine3D
  Height = 50
  Length = 47
  Placement = pos=(-9,-8,0) rot=(0,0,1;0rad)
  Width = 12
FEATURE [Part::Box] Box058  label="Cube051"
  AttacherType = Attacher::AttachEngine3D
  Height = 55
  Length = 53
  Placement = pos=(-12,-8,-2.5) rot=(0,0,1;0rad)
  Width = 11
FEATURE [Part::Cut] Cut045029
  Base = -> Box058
  Tool = -> Box057
FEATURE [Part::Box] Box059  label="Cube052"
  AttacherType = Attacher::AttachEngine3D
  Height = 5
  Length = 3
  Placement = pos=(35,-9,-4) rot=(0,0,1;0rad)
  Width = 12
FEATURE [Part::Cut] Cut045030
  Base = -> Cut045029
  Placement = pos=(-9,10,-58) rot=(1,0,0;1.5708rad)
  Tool = -> Box059
FEATURE [Part::Cut] Cut045031
  Base = -> Cut045029
  Placement = pos=(36.7,10,-56.7) rot=(1,0,0;1.5708rad)
  Tool = -> Box059
FEATURE [Part::Cut] Cut045032
  Base = -> Cut045029
  Placement = pos=(-6.4,10,-7.2) rot=(1,0,0;1.5708rad)
  Tool = -> Box059
FEATURE [Part::Cut] Cut045033
  Base = -> Cut045029
  Placement = pos=(21.5,10,-7.2) rot=(1,0,0;1.5708rad)
  Tool = -> Box059
FEATURE [Part::MultiFuse] Fusion126
  Shapes = -> [Cut045030,Cut045033,Cut045031,Cut045032]
FEATURE [Part::Mirroring] Part__Mirroring008  label="Hex Holes001"
  Base = (0,0,0)
  Normal = (1,0,0)
  Placement = pos=(27,0,-6) rot=(0,0,1;0rad)
  Source = -> Fusion126
FEATURE [Part::Box] Box060  label="Cube053"
  AttacherType = Attacher::AttachEngine3D
  Height = 5
  Length = 2
  Placement = pos=(37.5,-9,-2) rot=(0,0,1;0rad)
  Width = 12
FEATURE [Part::Box] Box061  label="Battery Base001"
  AttacherType = Attacher::AttachEngine3D
  Height = 50
  Length = 55
  Placement = pos=(-13,3,-1) rot=(0,0,1;0rad)
  Width = 7
FEATURE [Part::Cylinder] Cylinder097  label="Cylinder193"
  Angle = 360
  AttacherType = Attacher::AttachEngine3D
  Height = 42
  Radius = 4.8
FEATURE [Part::Cylinder] Cylinder098  label="Cylinder194"
  Angle = 360
  AttacherType = Attacher::AttachEngine3D
  Height = 1.6
  Placement = pos=(0,0,42) rot=(0,0,1;0rad)
  Radius = 1.65
FEATURE [Part::Fuse] Fusion127
  Base = -> Cylinder097
  Placement = pos=(2,0,0) rot=(0,0,1;0rad)
  Tool = -> Cylinder098
FEATURE [Part::Cylinder] Cylinder099  label="Cylinder195"
  Angle = 360
  AttacherType = Attacher::AttachEngine3D
  Height = 42
  Radius = 4.8
FEATURE [Part::Cylinder] Cylinder100  label="Cylinder196"
  Angle = 360
  AttacherType = Attacher::AttachEngine3D
  Height = 1.6
  Placement = pos=(0,0,42) rot=(0,0,1;0rad)
  Radius = 1.65
FEATURE [Part::Fuse] Fusion128
  Base = -> Cylinder099
  Placement = pos=(12,0,0) rot=(0,0,1;0rad)
  Tool = -> Cylinder100
FEATURE [Part::Cylinder] Cylinder101  label="Cylinder197"
  Angle = 360
  AttacherType = Attacher::AttachEngine3D
  Height = 42
  Radius = 4.8
FEATURE [Part::Cylinder] Cylinder102  label="Cylinder198"
  Angle = 360
  AttacherType = Attacher::AttachEngine3D
  Height = 1.6
  Placement = pos=(0,0,42) rot=(0,0,1;0rad)
  Radius = 1.65
FEATURE [Part::Fuse] Fusion129
  Base = -> Cylinder101
  Placement = pos=(22,0,0) rot=(0,0,1;0rad)
  Tool = -> Cylinder102
FEATURE [Part::Cylinder] Cylinder103  label="Cylinder199"
  Angle = 360
  AttacherType = Attacher::AttachEngine3D
  Height = 42
  Radius = 4.8
FEATURE [Part::Cylinder] Cylinder104  label="Cylinder200"
  Angle = 360
  AttacherType = Attacher::AttachEngine3D
  Height = 1.6
  Placement = pos=(0,0,42) rot=(0,0,1;0rad)
  Radius = 1.65
FEATURE [Part::Fuse] Fusion130
  Base = -> Cylinder103
  Placement = pos=(32,0,0) rot=(0,0,1;0rad)
  Tool = -> Cylinder104
FEATURE [Part::Cylinder] Cylinder105  label="Cylinder201"
  Angle = 360
  AttacherType = Attacher::AttachEngine3D
  Height = 42
  Radius = 4.8
FEATURE [Part::Cylinder] Cylinder106  label="Cylinder202"
  Angle = 360
  AttacherType = Attacher::AttachEngine3D
  Height = 1.6
  Placement = pos=(0,0,42) rot=(0,0,1;0rad)
  Radius = 1.65
FEATURE [Part::Fuse] Fusion131
  Base = -> Cylinder105
  Placement = pos=(-8,0,0) rot=(0,0,1;0rad)
  Tool = -> Cylinder106
FEATURE [Part::MultiFuse] Fusion132  label="AAA Batts002"
  Placement = pos=(2,0,2) rot=(0,0,1;0rad)
  Shapes = -> [Fusion131,Fusion127,Fusion128,Fusion129,Fusion130]
FEATURE [Part::Cut] Cut045034
  Base = -> Box061
  Tool = -> Fusion132
FEATURE [Part::Box] Box062  label="Cube054"
  AttacherType = Attacher::AttachEngine3D
  Height = 2.5
  Length = 55
  Placement = pos=(-13,-9,-1) rot=(0,0,1;0rad)
  Width = 12
FEATURE [Part::Box] Box063  label="Cube055"
  AttacherType = Attacher::AttachEngine3D
  Height = 2.5
  Length = 55
  Placement = pos=(-13,-9,46.5) rot=(0,0,1;0rad)
  Width = 12
FEATURE [Part::Box] Box064  label="Cube056"
  AttacherType = Attacher::AttachEngine3D
  Height = 50
  Length = 2.5
  Placement = pos=(-13,-9,-1) rot=(0,0,1;0rad)
  Width = 12
FEATURE [Part::Box] Box065  label="Cube057"
  AttacherType = Attacher::AttachEngine3D
  Height = 50
  Length = 2.5
  Placement = pos=(39.5,-9,-1) rot=(0,0,1;0rad)
  Width = 12
FEATURE [Part::MultiFuse] Fusion133
  Shapes = -> [Box062,Box064,Box065,Box063]
FEATURE [Part::Box] Box066  label="Cube058"
  AttacherType = Attacher::AttachEngine3D
  Height = 5
  Length = 2
  Placement = pos=(-10.5,-9,46) rot=(0,0,1;0rad)
  Width = 12
FEATURE [Part::Box] Box067  label="Cube059"
  AttacherType = Attacher::AttachEngine3D
  Height = 5
  Length = 2
  Placement = pos=(-10.5,-9,-2) rot=(0,0,1;0rad)
  Width = 12
FEATURE [Part::MultiFuse] Fusion134
  Shapes = -> [Box067,Box066,Box060,Box048]
FEATURE [Part::MultiFuse] Fusion135
  Shapes = -> [Box045,Box046,Box047,Box049]
FEATURE [Part::Cut] Cut045035
  Base = -> Fusion133
  Tool = -> Fusion134
FEATURE [Part::Cut] Cut045036
  Base = -> Cut045035
  Tool = -> Fusion135
FEATURE [Part::Cylinder] Cylinder107  label="Cylinder203"
  Angle = 360
  AttacherType = Attacher::AttachEngine3D
  Height = 14.5
  Placement = pos=(-43.6,-2.4,-15) rot=(0,0,1;0rad)
  Radius = 0.8
FEATURE [Part::Cylinder] Cylinder108  label="Cylinder204"
  Angle = 360
  AttacherType = Attacher::AttachEngine3D
  Height = 14.5
  Placement = pos=(-43.6,-13.8,-15) rot=(0,0,1;0rad)
  Radius = 0.8
FEATURE [Part::Fuse] Fusion136
  Base = -> Cut045034
  Tool = -> Cut045036
FEATURE [Part::Box] Box068  label="Cube060"
  AttacherType = Attacher::AttachEngine3D
  Height = 4
  Length = 12
  Placement = pos=(-50,-16.75,-14) rot=(0,0,1;0rad)
  Width = 26.75
FEATURE [Part::Chamfer] Chamfer002
  Base = -> Box068
  Edges = 1 edges r=7: [Edge3]
FEATURE [Part::Cone] Cone004
  Angle = 360
  AttacherType = Attacher::AttachEngine3D
  Height = 1.5
  Placement = pos=(-43.6,-2.4,-10) rot=(0,0,1;0rad)
  Radius1 = 2.75
  Radius2 = 1.25
FEATURE [Part::Cone] Cone005
  Angle = 360
  AttacherType = Attacher::AttachEngine3D
  Height = 1.5
  Placement = pos=(-43.6,-13.8,-10) rot=(0,0,1;0rad)
  Radius1 = 2.75
  Radius2 = 1.25
FEATURE [Part::Fuse] Fusion137
  Base = -> Cone004
  Tool = -> Cone005
FEATURE [Part::Fuse] Fusion138
  Base = -> Chamfer002
  Tool = -> Fusion137
FEATURE [Part::Fuse] Fusion139
  Base = -> Cylinder107
  Tool = -> Cylinder108
FEATURE [Part::Cut] Cut045037
  Base = -> Fusion138
  Tool = -> Fusion139
FEATURE [Part::Cylinder] Cylinder109  label="Cylinder205"
  Angle = 360
  AttacherType = Attacher::AttachEngine3D
  Height = 14.5
  Placement = pos=(-43.6,-2.4,-15) rot=(0,0,1;0rad)
  Radius = 0.8
FEATURE [Part::Cylinder] Cylinder110  label="Cylinder206"
  Angle = 360
  AttacherType = Attacher::AttachEngine3D
  Height = 14.5
  Placement = pos=(-43.6,-13.8,-15) rot=(0,0,1;0rad)
  Radius = 0.8
FEATURE [Part::Box] Box069  label="Cube061"
  AttacherType = Attacher::AttachEngine3D
  Height = 4
  Length = 12
  Placement = pos=(-50,-16.75,-14) rot=(0,0,1;0rad)
  Width = 26.75
FEATURE [Part::Chamfer] Chamfer003
  Base = -> Box069
  Edges = 1 edges r=7: [Edge3]
FEATURE [Part::Cone] Cone006
  Angle = 360
  AttacherType = Attacher::AttachEngine3D
  Height = 1.5
  Placement = pos=(-43.6,-2.4,-10) rot=(0,0,1;0rad)
  Radius1 = 2.75
  Radius2 = 1.25
FEATURE [Part::Cone] Cone007
  Angle = 360
  AttacherType = Attacher::AttachEngine3D
  Height = 1.5
  Placement = pos=(-43.6,-13.8,-10) rot=(0,0,1;0rad)
  Radius1 = 2.75
  Radius2 = 1.25
FEATURE [Part::Fuse] Fusion140
  Base = -> Cone006
  Tool = -> Cone007
FEATURE [Part::Fuse] Fusion141
  Base = -> Chamfer003
  Tool = -> Fusion140
FEATURE [Part::Fuse] Fusion142
  Base = -> Cylinder109
  Tool = -> Cylinder110
FEATURE [Part::Cut] Cut045038
  Base = -> Fusion141
  Tool = -> Fusion142
FEATURE [Part::Mirroring] Part__Mirroring009  label="Cut045028 (Mirror #6)001"
  Base = (0,0,0)
  Normal = (1,0,0)
  Placement = pos=(27,0,0) rot=(0,0,1;0rad)
  Source = -> Cut045038
FEATURE [Part::Cut] Cut045039
  Base = -> Box050
  Tool = -> Fusion120
FEATURE [Part::Cut] Cut045040
  Base = -> Box051
  Tool = -> Fusion122
FEATURE [Part::MultiFuse] Fusion143
  Shapes = -> [Box054,Box055,Box056]
FEATURE [Part::Fuse] Fusion144
  Base = -> Fusion136
  Tool = -> Fusion143
FEATURE [Part::MultiFuse] Fusion145
  Shapes = -> [Fusion144,Cut045040,Cut045039]
FEATURE [Part::MultiFuse] Fusion146
  Shapes = -> [Fusion145,Part__Mirroring009,Cut045037]
FEATURE [Part::Cut] Cut045041
  Base = -> Fusion146
  Tool = -> Fusion117
FEATURE [Part::Cut] Cut045042
  Base = -> Cut045041
  Tool = -> Fusion118
FEATURE [Part::Cut] Cut045043
  Base = -> Cut045042
  Tool = -> Part__Mirroring007
FEATURE [Part::Cut] Cut045044
  Base = -> Cut045043
  Tool = -> Part__Mirroring008
FEATURE [Part::MultiFuse] Fusion147
  Shapes = -> [Cut045044,Box053,Box052]
FEATURE [Part::Chamfer] Chamfer004
  Base = -> Fusion147
  Edges = 1 edges r=25: [Edge43]
FEATURE [Part::Chamfer] Chamfer005
  Base = -> Chamfer004
  Edges = 1 edges r=25: [Edge225]
FEATURE [Part::Chamfer] Chamfer006
  Base = -> Chamfer005
  Edges = 1 edges r=30: [Edge58]
FEATURE [Part::Chamfer] Chamfer007
  Base = -> Chamfer006
  Edges = 1 edges r=30: [Edge148]
FEATURE [Part::Fillet] Fillet
  Base = -> Chamfer007
  Edges = 1 edges r=2: [Edge233]
FEATURE [Part::Fillet] Fillet001
  Base = -> Fillet
  Edges = 1 edges r=2: [Edge6]
FEATURE [Part::Fillet] Fillet002
  Base = -> Fillet001
  Edges = 1 edges r=2: [Edge2]
FEATURE [Part::Fillet] Fillet003
  Base = -> Fillet002
  Edges = 1 edges r=2: [Edge357]
FEATURE [Part::Fillet] Fillet004
  Base = -> Fillet003
  Edges = 1 edges r=2: [Edge6]
FEATURE [Part::Fillet] Fillet005
  Base = -> Fillet004
  Edges = 1 edges r=2: [Edge2]
FEATURE [Part::Fillet] Fillet006
  Base = -> Fillet005
  Edges = 1 edges r=2: [Edge407]
FEATURE [Part::Fillet] Fillet007
  Base = -> Fillet006
  Edges = 1 edges r=2: [Edge2]
FEATURE [Part::Fillet] Fillet008
  Base = -> Fillet007
  Edges = 1 edges r=2: [Edge369]
FEATURE [Part::Fillet] Fillet009
  Base = -> Fillet008
  Edges = 1 edges r=2: [Edge2]
FEATURE [Part::Cylinder] Cylinder111  label="Cylinder207"
  Angle = 360
  AttacherType = Attacher::AttachEngine3D
  Height = 28
  Placement = pos=(45,6,47) rot=(0.707107,0,0.707107;4.01426rad)
  Radius = 0.5
FEATURE [Part::Cylinder] Cylinder112  label="Cylinder208"
  Angle = 360
  AttacherType = Attacher::AttachEngine3D
  Height = 28
  Placement = pos=(66,6,26) rot=(0.707107,0,0.707107;4.01426rad)
  Radius = 0.5
FEATURE [Part::Cut] Cut045045
  Base = -> Fillet009
  Tool = -> Cylinder111
FEATURE [Part::Cut] Cut045046
  Base = -> Cut045045
  Tool = -> Cylinder112
FEATURE [Part::Cylinder] Cylinder113  label="Cylinder209"
  Angle = 360
  AttacherType = Attacher::AttachEngine3D
  Height = 28
  Placement = pos=(66,6,26) rot=(0.707107,0,0.707107;4.01426rad)
  Radius = 0.5
FEATURE [Part::Mirroring] Part__Mirroring010  label="Cylinder137 (Mirror #7)"
  Base = (0,0,0)
  Normal = (1,0,0)
  Placement = pos=(27,0,0) rot=(0,0,1;0rad)
  Source = -> Cylinder113
FEATURE [Part::Cylinder] Cylinder114  label="Cylinder210"
  Angle = 360
  AttacherType = Attacher::AttachEngine3D
  Height = 28
  Placement = pos=(45,6,47) rot=(0.707107,0,0.707107;4.01426rad)
  Radius = 0.5
FEATURE [Part::Mirroring] Part__Mirroring011  label="Cylinder138 (Mirror #8)"
  Base = (0,0,0)
  Normal = (1,0,0)
  Placement = pos=(27,0,0) rot=(0,0,1;0rad)
  Source = -> Cylinder114
FEATURE [Part::Cut] Cut045047
  Base = -> Cut045046
  Tool = -> Part__Mirroring010
FEATURE [Part::Cut] Cut045048  label="Old Layout"
  Base = -> Cut045047
  Tool = -> Part__Mirroring011
FEATURE [Part::Cylinder] Cylinder115  label="Arduino Cylinder191"
  Angle = 360
  AttacherType = Attacher::AttachEngine3D
  Height = 28
  Placement = pos=(4,11,-8.6) rot=(1,0,0;1.5708rad)
  Radius = 1.6
FEATURE [Part::Cylinder] Cylinder116  label="Arduino Cylinder192"
  Angle = 360
  AttacherType = Attacher::AttachEngine3D
  Height = 28
  Placement = pos=(31.9,11,-8.6) rot=(1,0,0;1.5708rad)
  Radius = 1.6
FEATURE [Part::Cylinder] Cylinder117  label="Arduino Cylinder193"
  Angle = 360
  AttacherType = Attacher::AttachEngine3D
  Height = 28
  Placement = pos=(-11.2,11,-59.4) rot=(1,0,0;1.5708rad)
  Radius = 1.6
FEATURE [Part::Cylinder] Cylinder118  label="Arduino Cylinder194"
  Angle = 360
  AttacherType = Attacher::AttachEngine3D
  Height = 28
  Placement = pos=(37.2,11,-60.5) rot=(1,0,0;1.5708rad)
  Radius = 1.6
FEATURE [Part::Cylinder] Cylinder119  label="Arduino Cylinder195"
  Angle = 360
  AttacherType = Attacher::AttachEngine3D
  Height = 2.5
  Placement = pos=(4,13,-8.6) rot=(1,0,0;1.5708rad)
  Radius = 4
FEATURE [Part::Feature] Box014001
  Placement = pos=(3.88157,4,-2.89487) rot=(0,1,0;1.0472rad)
  shape: bbox 13.66 x 10 x 13.66 mm, 6 faces (baked)
FEATURE [Part::Feature] Box014002
  Placement = pos=(8.88157,4,-5.64487) rot=(0,1,0;2.0944rad)
  shape: bbox 13.66 x 10 x 13.66 mm, 6 faces (baked)
FEATURE [Part::Feature] Box014003
  Placement = pos=(9,4,-11.35) rot=(0,1,0;3.14159rad)
  shape: bbox 10 x 10 x 10 mm, 6 faces (baked)
FEATURE [Part::Feature] Box014004
  Placement = pos=(4.11843,4,-14.3051) rot=(0,1,0;4.18879rad)
  shape: bbox 13.66 x 10 x 13.66 mm, 6 faces (baked)
FEATURE [Part::Feature] Box014005
  Placement = pos=(-0.88157,4,-11.5551) rot=(0,-1,0;1.0472rad)
  shape: bbox 13.66 x 10 x 13.66 mm, 6 faces (baked)
FEATURE [Part::MultiFuse] Fusion148
  Shapes = -> [Box014001,Box014002,Box014004,Box014003,Box014005,Box014]
FEATURE [Part::Cut] Cut045049  label="M3 Nut004"
  Base = -> Cylinder119
  Placement = pos=(0,-3,0) rot=(0,0,1;0rad)
  Tool = -> Fusion148
FEATURE [Part::Box] Box014006  label="Not used Cube001"
  AttacherType = Attacher::AttachEngine3D
  Height = 10
  Length = 10
  Placement = pos=(-1,4,-5.85) rot=(0,0,1;0rad)
  Width = 10
FEATURE [Part::Cylinder] Cylinder120  label="Arduino Cylinder196"
  Angle = 360
  AttacherType = Attacher::AttachEngine3D
  Height = 2.5
  Placement = pos=(4,13,-8.6) rot=(1,0,0;1.5708rad)
  Radius = 4
FEATURE [Part::Feature] Box014007
  Placement = pos=(3.88157,4,-2.89487) rot=(0,1,0;1.0472rad)
  shape: bbox 13.66 x 10 x 13.66 mm, 6 faces (baked)
FEATURE [Part::Feature] Box014008
  Placement = pos=(8.88157,4,-5.64487) rot=(0,1,0;2.0944rad)
  shape: bbox 13.66 x 10 x 13.66 mm, 6 faces (baked)
FEATURE [Part::Feature] Box014009
  Placement = pos=(9,4,-11.35) rot=(0,1,0;3.14159rad)
  shape: bbox 10 x 10 x 10 mm, 6 faces (baked)
FEATURE [Part::Feature] Box014010
  Placement = pos=(4.11843,4,-14.3051) rot=(0,1,0;4.18879rad)
  shape: bbox 13.66 x 10 x 13.66 mm, 6 faces (baked)
FEATURE [Part::Feature] Box014011
  Placement = pos=(-0.88157,4,-11.5551) rot=(0,-1,0;1.0472rad)
  shape: bbox 13.66 x 10 x 13.66 mm, 6 faces (baked)
FEATURE [Part::MultiFuse] Fusion149
  Shapes = -> [Box014007,Box014008,Box014010,Box014009,Box014011,Box014006]
FEATURE [Part::Cut] Cut045050  label="M3 Nut005"
  Base = -> Cylinder120
  Placement = pos=(27.9,-3,0) rot=(0,0,1;0rad)
  Tool = -> Fusion149
FEATURE [Part::Box] Box014012  label="Not used Cube002"
  AttacherType = Attacher::AttachEngine3D
  Height = 10
  Length = 10
  Placement = pos=(-1,4,-5.85) rot=(0,0,1;0rad)
  Width = 10
FEATURE [Part::Cylinder] Cylinder121  label="Arduino Cylinder197"
  Angle = 360
  AttacherType = Attacher::AttachEngine3D
  Height = 2.5
  Placement = pos=(4,13,-8.6) rot=(1,0,0;1.5708rad)
  Radius = 4
FEATURE [Part::Feature] Box014013
  Placement = pos=(3.88157,4,-2.89487) rot=(0,1,0;1.0472rad)
  shape: bbox 13.66 x 10 x 13.66 mm, 6 faces (baked)
FEATURE [Part::Feature] Box014014
  Placement = pos=(8.88157,4,-5.64487) rot=(0,1,0;2.0944rad)
  shape: bbox 13.66 x 10 x 13.66 mm, 6 faces (baked)
FEATURE [Part::Feature] Box014015
  Placement = pos=(9,4,-11.35) rot=(0,1,0;3.14159rad)
  shape: bbox 10 x 10 x 10 mm, 6 faces (baked)
FEATURE [Part::Feature] Box014016
  Placement = pos=(4.11843,4,-14.3051) rot=(0,1,0;4.18879rad)
  shape: bbox 13.66 x 10 x 13.66 mm, 6 faces (baked)
FEATURE [Part::Feature] Box014017
  Placement = pos=(-0.88157,4,-11.5551) rot=(0,-1,0;1.0472rad)
  shape: bbox 13.66 x 10 x 13.66 mm, 6 faces (baked)
FEATURE [Part::MultiFuse] Fusion150
  Shapes = -> [Box014013,Box014014,Box014016,Box014015,Box014017,Box014012]
FEATURE [Part::Cut] Cut045051  label="M3 Nut006"
  Base = -> Cylinder121
  Placement = pos=(-15.2,-3,-50.8) rot=(0,0,1;0rad)
  Tool = -> Fusion150
FEATURE [Part::Box] Box014018  label="Not used Cube003"
  AttacherType = Attacher::AttachEngine3D
  Height = 10
  Length = 10
  Placement = pos=(-1,4,-5.85) rot=(0,0,1;0rad)
  Width = 10
FEATURE [Part::Cylinder] Cylinder122  label="Arduino Cylinder198"
  Angle = 360
  AttacherType = Attacher::AttachEngine3D
  Height = 2.5
  Placement = pos=(4,13,-8.6) rot=(1,0,0;1.5708rad)
  Radius = 4
FEATURE [Part::Feature] Box014019
  Placement = pos=(3.88157,4,-2.89487) rot=(0,1,0;1.0472rad)
  shape: bbox 13.66 x 10 x 13.66 mm, 6 faces (baked)
FEATURE [Part::Feature] Box014020
  Placement = pos=(8.88157,4,-5.64487) rot=(0,1,0;2.0944rad)
  shape: bbox 13.66 x 10 x 13.66 mm, 6 faces (baked)
FEATURE [Part::Feature] Box014021
  Placement = pos=(9,4,-11.35) rot=(0,1,0;3.14159rad)
  shape: bbox 10 x 10 x 10 mm, 6 faces (baked)
FEATURE [Part::Feature] Box014022
  Placement = pos=(4.11843,4,-14.3051) rot=(0,1,0;4.18879rad)
  shape: bbox 13.66 x 10 x 13.66 mm, 6 faces (baked)
FEATURE [Part::Feature] Box014023
  Placement = pos=(-0.88157,4,-11.5551) rot=(0,-1,0;1.0472rad)
  shape: bbox 13.66 x 10 x 13.66 mm, 6 faces (baked)
FEATURE [Part::MultiFuse] Fusion151
  Shapes = -> [Box014019,Box014020,Box014022,Box014021,Box014023,Box014018]
FEATURE [Part::Cut] Cut045052  label="M3 Nut007"
  Base = -> Cylinder122
  Placement = pos=(33.2,-3,-51.9) rot=(0,0,1;0rad)
  Tool = -> Fusion151
FEATURE [Part::Box] Box014024  label="Cube062"
  AttacherType = Attacher::AttachEngine3D
  Height = 67
  Length = 65
  Placement = pos=(-16,-13,-6) rot=(0,0,1;0rad)
  Width = 8
FEATURE [Part::Cut] Cut045053  label="BAtt Holder"
  Base = -> Fusion110
  Tool = -> Box014024
FEATURE [Part::Cylinder] Cylinder123  label="Cylinder211"
  Angle = 360
  AttacherType = Attacher::AttachEngine3D
  Height = 28
  Placement = pos=(45,6,47) rot=(0.707107,0,0.707107;4.01426rad)
  Radius = 0.5
FEATURE [Part::Cylinder] Cylinder124  label="Cylinder212"
  Angle = 360
  AttacherType = Attacher::AttachEngine3D
  Height = 28
  Placement = pos=(66,6,26) rot=(0.707107,0,0.707107;4.01426rad)
  Radius = 0.5
FEATURE [Part::Cylinder] Cylinder125  label="Cylinder213"
  Angle = 360
  AttacherType = Attacher::AttachEngine3D
  Height = 28
  Placement = pos=(45,6,47) rot=(0.707107,0,0.707107;4.01426rad)
  Radius = 0.5
FEATURE [Part::Cylinder] Cylinder126  label="Cylinder214"
  Angle = 360
  AttacherType = Attacher::AttachEngine3D
  Height = 28
  Placement = pos=(66,6,26) rot=(0.707107,0,0.707107;4.01426rad)
  Radius = 0.5
FEATURE [Part::Mirroring] Part__Mirroring012  label="Cylinder211 (Mirror #13)"
  Base = (0,0,0)
  Normal = (1,0,0)
  Placement = pos=(27,0,0) rot=(0,0,1;0rad)
  Source = -> Cylinder125
FEATURE [Part::Mirroring] Part__Mirroring013  label="Cylinder212 (Mirror #14)"
  Base = (0,0,0)
  Normal = (1,0,0)
  Placement = pos=(27,0,0) rot=(0,0,1;0rad)
  Source = -> Cylinder126
FEATURE [Part::Chamfer] Chamfer008
  Base = -> Fusion104
  Edges = 1 edges r=0.5: [Edge67]
FEATURE [Part::Chamfer] Chamfer009  label="Switch Mount"
  Base = -> Chamfer008
  Edges = 1 edges r=0.5: [Edge6]
FEATURE [Part::Box] Box014025  label="Cube063"
  AttacherType = Attacher::AttachEngine3D
  Height = 14
  Length = 15
  Placement = pos=(-46,4,-27) rot=(0,0,1;0rad)
  Width = 3
FEATURE [Part::Cylinder] Cylinder127  label="Cylinder215"
  Angle = 360
  AttacherType = Attacher::AttachEngine3D
  Height = 10
  Placement = pos=(-39,9,-22) rot=(1,0,0;1.5708rad)
  Radius = 3
FEATURE [Part::Box] Box014026  label="Cube064"
  AttacherType = Attacher::AttachEngine3D
  Height = 9.5
  Length = 15
  Placement = pos=(-46,0,-27) rot=(0,0,1;0rad)
  Width = 3
FEATURE [Part::Cylinder] Cylinder128  label="Cylinder216"
  Angle = 360
  AttacherType = Attacher::AttachEngine3D
  Height = 14
  Placement = pos=(-39,11,-22) rot=(1,0,0;1.5708rad)
  Radius = 1.5
FEATURE [Part::Cut] Cut045054
  Base = -> Box014025
  Tool = -> Cylinder127
FEATURE [Part::Cylinder] Cylinder129  label="Cylinder217"
  Angle = 360
  AttacherType = Attacher::AttachEngine3D
  Height = 14
  Placement = pos=(-39,11,-22) rot=(1,0,0;1.5708rad)
  Radius = 1.5
FEATURE [Part::Cut] Cut045055  label="Printed Washer"
  Base = -> Box014026
  Tool = -> Cylinder128
FEATURE [Part::Box] Box014027  label="Cube065"
  AttacherType = Attacher::AttachEngine3D
  Height = 23
  Length = 22
  Placement = pos=(-46,4,0) rot=(0,0,1;0rad)
  Width = 3
FEATURE [Part::Cylinder] Cylinder130  label="Cylinder218"
  Angle = 360
  AttacherType = Attacher::AttachEngine3D
  Height = 14
  Placement = pos=(-38,11,4) rot=(1,0,0;1.5708rad)
  Radius = 1.5
FEATURE [Part::Cylinder] Cylinder131  label="Cylinder219"
  Angle = 360
  AttacherType = Attacher::AttachEngine3D
  Height = 14
  Placement = pos=(-28,11,4) rot=(1,0,0;1.5708rad)
  Radius = 1.5
FEATURE [Part::Cylinder] Cylinder132  label="Cylinder220"
  Angle = 360
  AttacherType = Attacher::AttachEngine3D
  Height = 14.5
  Placement = pos=(-53.76,-13.8,-18) rot=(0,0,1;0rad)
  Radius = 0.8
FEATURE [Part::Box] Box014028  label="Cube066"
  AttacherType = Attacher::AttachEngine3D
  Height = 4
  Length = 19
  Placement = pos=(-57,-16.75,-17) rot=(0,0,1;0rad)
  Width = 8.75
FEATURE [Part::Cone] Cone008
  Angle = 360
  AttacherType = Attacher::AttachEngine3D
  Height = 1.5
  Placement = pos=(-53.76,-13.8,-13) rot=(0,0,1;0rad)
  Radius1 = 2.75
  Radius2 = 1.25
FEATURE [Part::Fuse] Fusion152
  Base = -> Fusion111
  Tool = -> Cone008
FEATURE [Part::Fuse] Fusion153
  Base = -> Fusion113
  Tool = -> Cylinder132
FEATURE [Part::Fuse] Fusion154
  Base = -> Box043
  Tool = -> Box014028
FEATURE [Part::Fuse] Fusion155
  Base = -> Cut045054
  Tool = -> Fusion154
FEATURE [Part::Fuse] Fusion156
  Base = -> Fusion152
  Tool = -> Fusion155
FEATURE [Part::Cut] Cut045056
  Base = -> Fusion156
  Tool = -> Fusion153
FEATURE [Part::Chamfer] Chamfer
  Base = -> Cut045056
  Edges = 1 edges r=6.99: [Edge15]
FEATURE [Part::Fillet] Fillet010
  Base = -> Chamfer
  Edges = 1 edges r=1: [Edge51]
FEATURE [Part::Fillet] Fillet011
  Base = -> Fillet010
  Edges = 1 edges r=1: [Edge11]
FEATURE [Part::Fillet] Fillet012
  Base = -> Fillet011
  Edges = 1 edges r=1: [Edge37]
FEATURE [Part::Fillet] Fillet013
  Base = -> Fillet012
  Edges = 1 edges r=5: [Edge54]
FEATURE [Part::Fillet] Fillet014
  Base = -> Fillet013
  Edges = 1 edges r=5: [Edge12]
